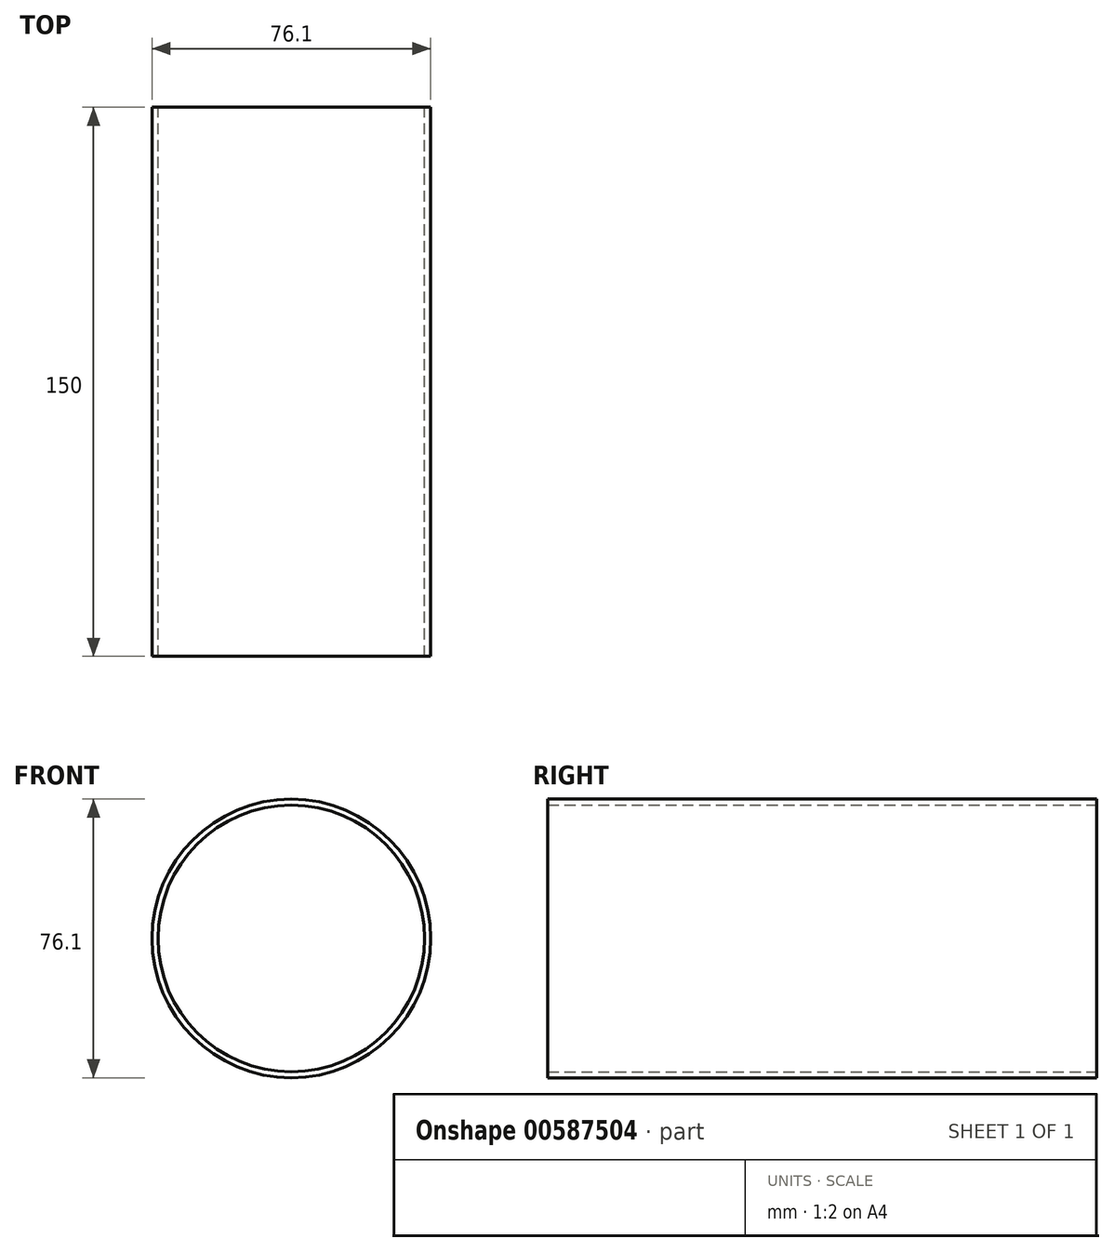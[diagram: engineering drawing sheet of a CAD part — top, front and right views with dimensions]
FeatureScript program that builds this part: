
annotation { "Feature Type Name" : "Feature", "Feature Type Description" : "" }
export const myFeature = defineFeature(function(context is Context, id is Id, definition is map)
    precondition{}
    {
        {
            var Q0;
            Q0=qCreatedBy(makeId("Front.planeOp"),FACE);
            var sketch = newSketch(context, id + "F0", { "sketchPlane" : qUnion([Q0])});
            skCircle(sketch, "E0", {"center": v(0, 0) * mm, "radius": 38.05 * mm});
            skCircle(sketch, "E1.0", {"center": v(0, 0) * mm, "radius": 36.4 * mm});
            skSolve(sketch);
        }
        {
            var Q0;
            Q0=makeQuery(id+"F0.imprint","IMPRINT",FACE,{"disambiguationData":[TD([[makeQuery(id+"F0.imprint","IMPRINT",EDGE,{"derivedFrom":sQuery(id+"F0.wireOp",EDGE,"E0")}),1.0]])]});
            extrude(context, id + "F1", {"entities" : qUnion([Q0]), "depth" : 150 * mm, "offsetDistance" : 25 * mm});
        }
    });
